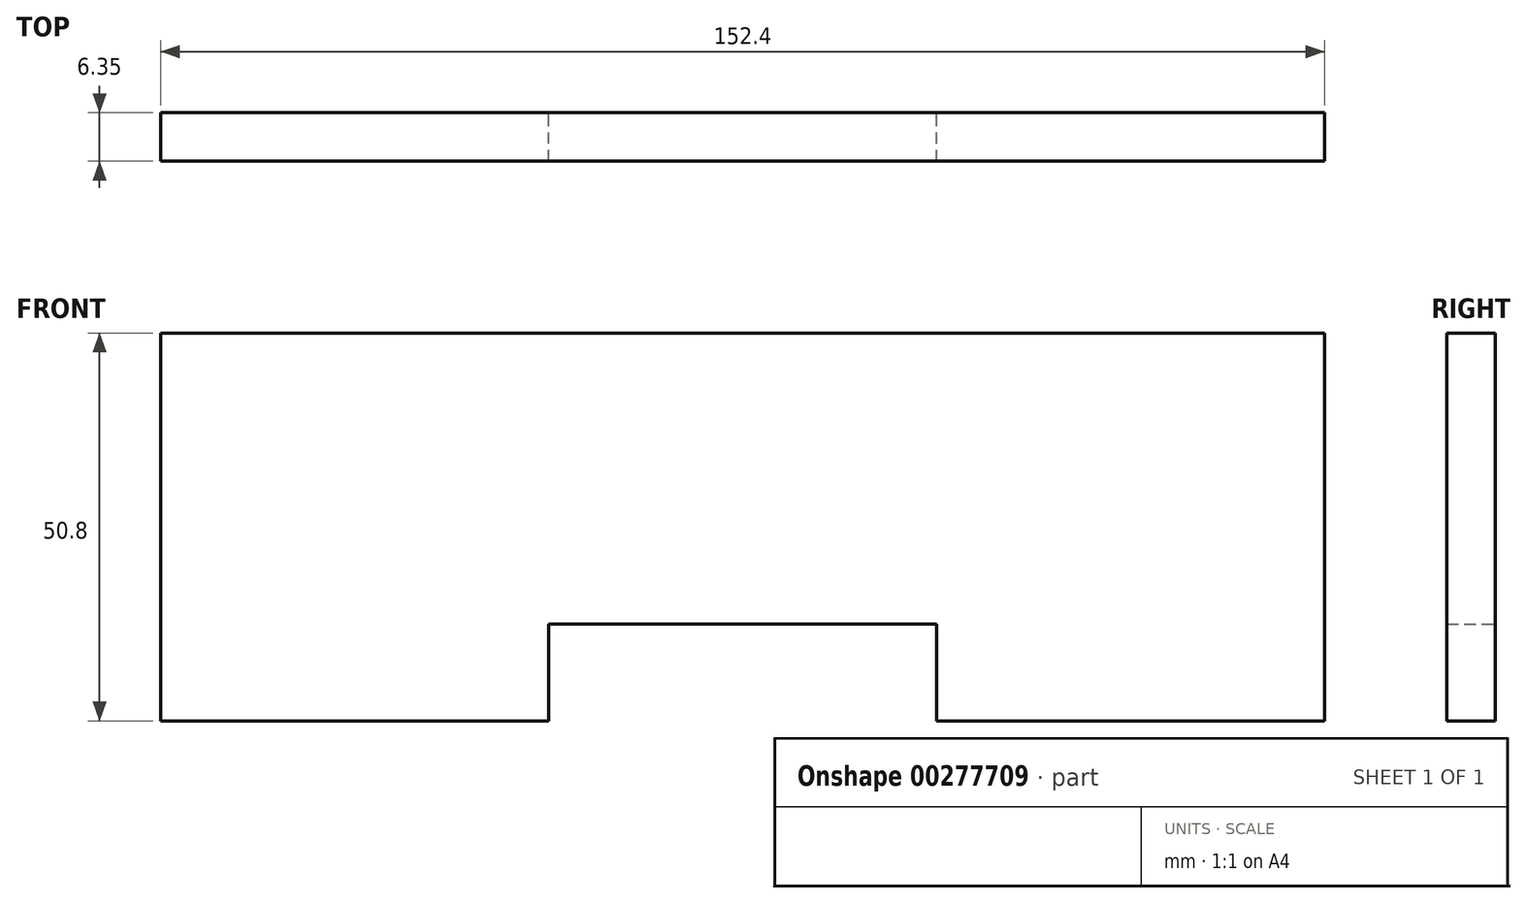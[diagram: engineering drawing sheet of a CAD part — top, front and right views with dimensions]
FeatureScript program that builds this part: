
annotation { "Feature Type Name" : "Feature", "Feature Type Description" : "" }
export const myFeature = defineFeature(function(context is Context, id is Id, definition is map)
    precondition{}
    {
        {
            var Q0;
            Q0=qCreatedBy(makeId("Front.planeOp"),FACE);
            var sketch = newSketch(context, id + "F0", { "sketchPlane" : qUnion([Q0])});
            skLineSegment(sketch, "E0", {"start": v(-55.16, 40.14) * mm, "end": v(-55.16, -10.66) * mm});
            skLineSegment(sketch, "E1", {"start": v(-55.16, -10.66) * mm, "end": v(-4.36, -10.66) * mm});
            skLineSegment(sketch, "E2", {"start": v(-4.36, -10.66) * mm, "end": v(-4.36, 2.04) * mm});
            skLineSegment(sketch, "E3", {"start": v(-4.36, 2.04) * mm, "end": v(46.44, 2.04) * mm});
            skLineSegment(sketch, "E4", {"start": v(46.44, 2.04) * mm, "end": v(46.44, -10.66) * mm});
            skLineSegment(sketch, "E5", {"start": v(46.44, -10.66) * mm, "end": v(97.24, -10.66) * mm});
            skLineSegment(sketch, "E6", {"start": v(97.24, -10.66) * mm, "end": v(97.24, 40.14) * mm});
            skLineSegment(sketch, "E7", {"start": v(97.24, 40.14) * mm, "end": v(-55.16, 40.14) * mm});
            skSolve(sketch);
        }
        {
            var Q0;
            Q0 = qSketchRegion(id + "F0", true);
            extrude(context, id + "F1", {"entities" : qUnion([Q0]), "depth" : 6.35 * mm});
        }
    });
